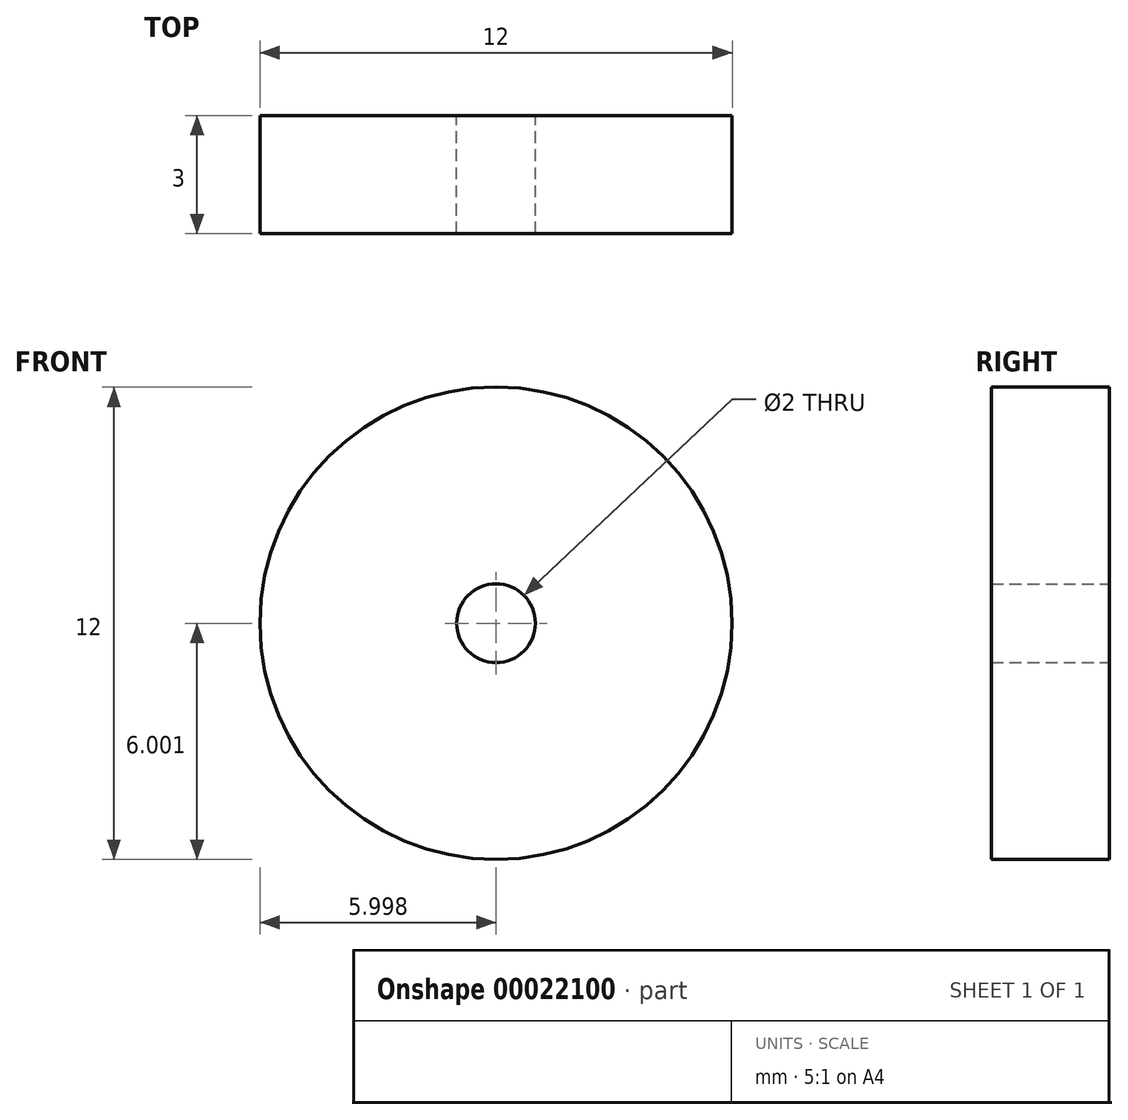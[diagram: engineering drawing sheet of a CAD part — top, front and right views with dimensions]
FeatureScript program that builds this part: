
annotation { "Feature Type Name" : "Feature", "Feature Type Description" : "" }
export const myFeature = defineFeature(function(context is Context, id is Id, definition is map)
    precondition{}
    {
        {
            var Q0;
            Q0=qCreatedBy(makeId("Front.planeOp"),FACE);
            var sketch = newSketch(context, id + "F0", { "sketchPlane" : qUnion([Q0])});
            skCircle(sketch, "E0", {"center": v(-27.04, 29.15) * mm, "radius": 6 * mm});
            skCircle(sketch, "E1", {"center": v(-27.04, 29.15) * mm, "radius": 1 * mm});
            skSolve(sketch);
        }
        {
            var Q0;
            Q0=makeQuery(id+"F0.imprint","IMPRINT",FACE,{"disambiguationData":[TD([[makeQuery(id+"F0.imprint","IMPRINT",EDGE,{"derivedFrom":sQuery(id+"F0.wireOp",EDGE,"E0")}),1.0]])]});
            extrude(context, id + "F1", {"entities" : qUnion([Q0]), "endBound" : BoundingType.SYMMETRIC, "depth" : 3 * mm});
        }
    });
